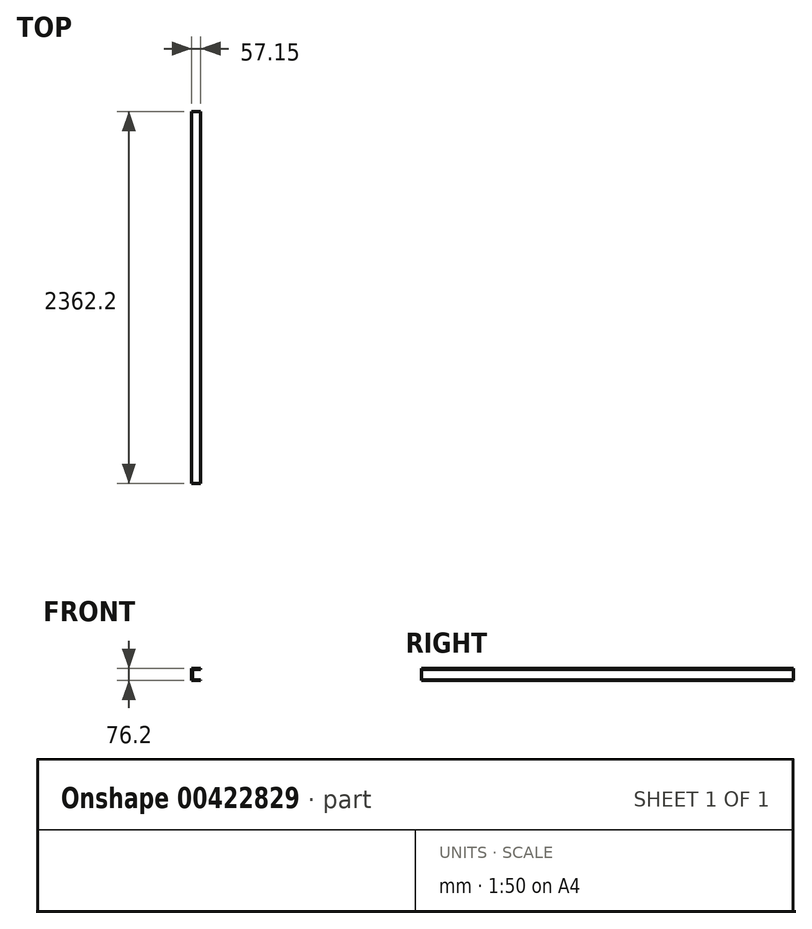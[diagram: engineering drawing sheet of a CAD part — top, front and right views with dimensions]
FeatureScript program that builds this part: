
annotation { "Feature Type Name" : "Feature", "Feature Type Description" : "" }
export const myFeature = defineFeature(function(context is Context, id is Id, definition is map)
    precondition{}
    {
        {
            var Q0;
            Q0=qCreatedBy(makeId("Front.planeOp"),FACE);
            var sketch = newSketch(context, id + "F0", { "sketchPlane" : qUnion([Q0])});
            skLineSegment(sketch, "E0.bottom", {"start": v(0, 0) * mm, "end": v(6.35, 0) * mm});
            skLineSegment(sketch, "E0.top", {"start": v(0, 76.2) * mm, "end": v(6.35, 76.2) * mm});
            skLineSegment(sketch, "E0.left", {"start": v(0, 0) * mm, "end": v(0, 76.2) * mm});
            skLineSegment(sketch, "E0.right", {"start": v(6.35, 0) * mm, "end": v(6.35, 76.2) * mm});
            skLineSegment(sketch, "E1.bottom", {"start": v(6.35, 76.2) * mm, "end": v(57.15, 76.2) * mm});
            skLineSegment(sketch, "E1.top", {"start": v(6.35, 71.44) * mm, "end": v(57.15, 71.44) * mm});
            skLineSegment(sketch, "E1.right", {"start": v(57.15, 76.2) * mm, "end": v(57.15, 71.44) * mm});
            skLineSegment(sketch, "E2.bottom", {"start": v(6.35, 0) * mm, "end": v(57.15, 0) * mm});
            skLineSegment(sketch, "E2.top", {"start": v(6.35, 4.76) * mm, "end": v(57.15, 4.76) * mm});
            skLineSegment(sketch, "E2.left", {"start": v(6.35, 0) * mm, "end": v(6.35, 4.76) * mm});
            skLineSegment(sketch, "E2.right", {"start": v(57.15, 0) * mm, "end": v(57.15, 4.76) * mm});
            skSolve(sketch);
        }
        {
            var Q0;
            {var subQ0=sQuery(id+"F0.wireOp",EDGE,"E1.bottom");Q0=makeQuery(id+"F0.imprint","IMPRINT",FACE,{"disambiguationData":[TD([[makeQuery(id+"F0.imprint","IMPRINT",EDGE,{"derivedFrom":subQ0}),-1.0]])]});}
            var Q1;
            Q1=makeQuery(id+"F0.imprint","IMPRINT",FACE,{"disambiguationData":[TD([[makeQuery(id+"F0.imprint","IMPRINT",EDGE,{"derivedFrom":sQuery(id+"F0.wireOp",EDGE,"E0.bottom")}),1.0]])]});
            var Q2;
            Q2=makeQuery(id+"F0.imprint","IMPRINT",FACE,{"disambiguationData":[TD([[makeQuery(id+"F0.imprint","IMPRINT",EDGE,{"derivedFrom":sQuery(id+"F0.wireOp",EDGE,"E2.bottom")}),1.0]])]});
            extrude(context, id + "F1", {"entities" : qUnion([Q0, Q1, Q2]), "endBound" : BoundingType.SYMMETRIC, "depth" : 2362.2 * mm});
        }
    });
